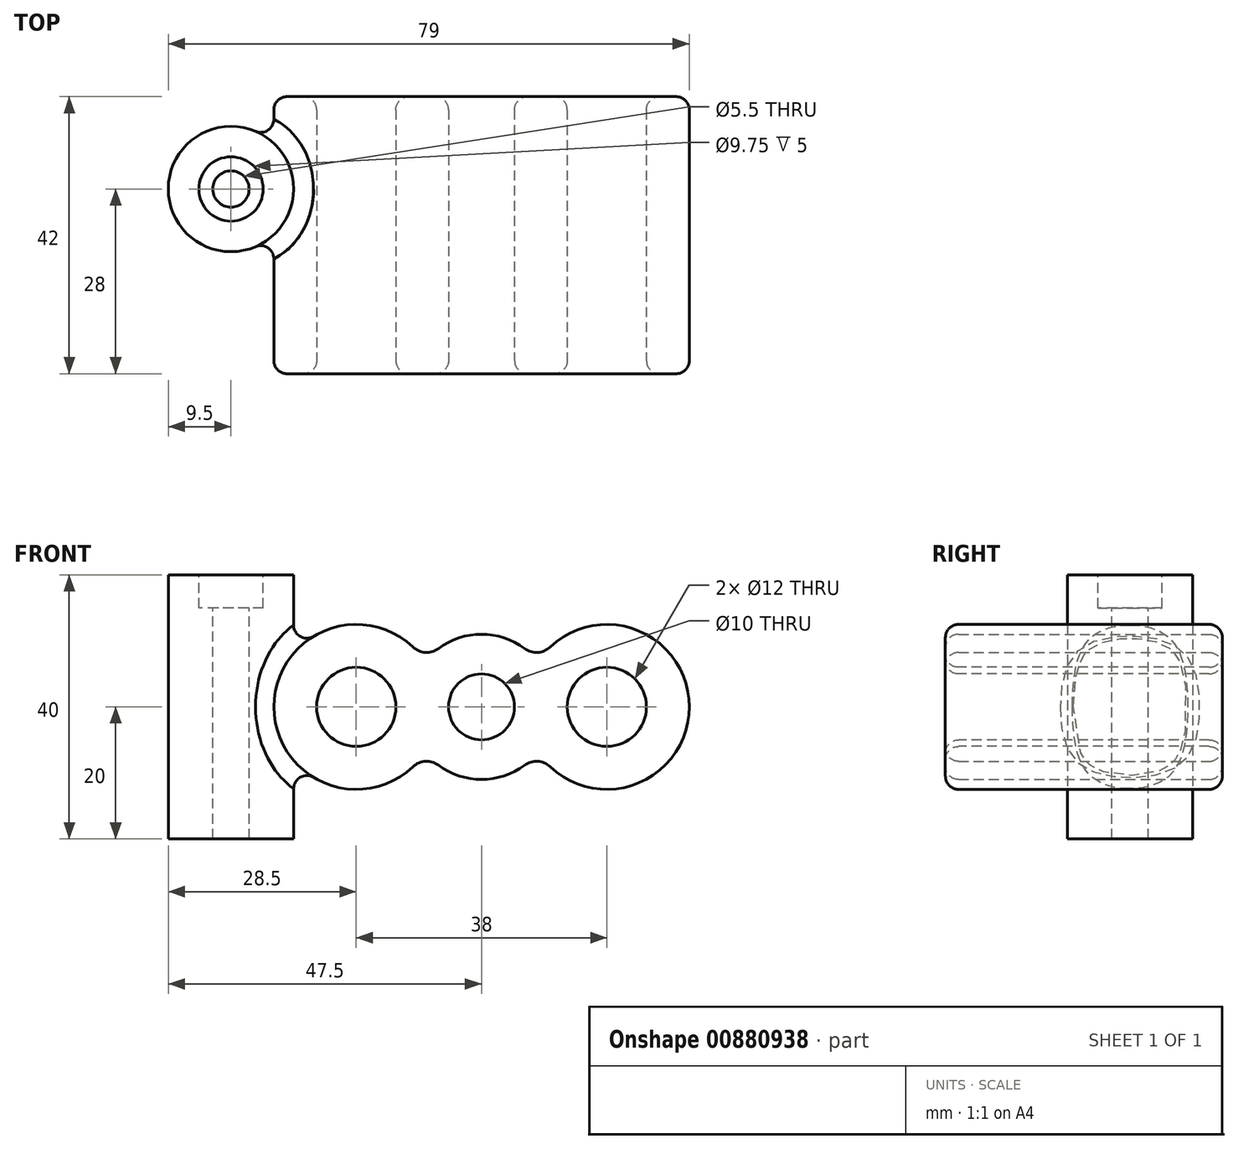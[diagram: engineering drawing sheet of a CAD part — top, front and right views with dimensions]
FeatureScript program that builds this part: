
annotation { "Feature Type Name" : "Feature", "Feature Type Description" : "" }
export const myFeature = defineFeature(function(context is Context, id is Id, definition is map)
    precondition{}
    {
        {
            var Q0;
            Q0=qCreatedBy(makeId("Front.planeOp"),FACE);
            var sketch = newSketch(context, id + "F0", { "sketchPlane" : qUnion([Q0])});
            skArc(sketch, "E0", {"start": v(-6.55, -8.84) * mm, "mid": v(0, -11) * mm, "end": v(6.55, -8.84) * mm});
            skArc(sketch, "E1", {"start": v(-10.4, 9.07) * mm, "mid": v(-31.5, 0) * mm, "end": v(-10.4, -9.07) * mm});
            skArc(sketch, "E2", {"start": v(10.4, -9.07) * mm, "mid": v(31.5, 0) * mm, "end": v(10.4, 9.07) * mm});
            skArc(sketch, "E3.trimOffspring", {"start": v(6.55, 8.84) * mm, "mid": v(0, 11) * mm, "end": v(-6.55, 8.84) * mm});
            skPoint(sketch, "E4.visualSharp", {"position": v(-8.57, -6.9) * mm});
            skArc(sketch, "E4.filletArc", {"start": v(-6.55, -8.84) * mm, "mid": v(-8.52, -8.25) * mm, "end": v(-10.4, -9.07) * mm});
            skPoint(sketch, "E5.visualSharp", {"position": v(8.57, -6.9) * mm});
            skArc(sketch, "E5.filletArc", {"start": v(10.4, -9.07) * mm, "mid": v(8.52, -8.25) * mm, "end": v(6.55, -8.84) * mm});
            skPoint(sketch, "E6.visualSharp", {"position": v(8.57, 6.9) * mm});
            skArc(sketch, "E6.filletArc", {"start": v(6.55, 8.84) * mm, "mid": v(8.52, 8.25) * mm, "end": v(10.4, 9.07) * mm});
            skPoint(sketch, "E7.visualSharp", {"position": v(-8.57, 6.9) * mm});
            skArc(sketch, "E7.filletArc", {"start": v(-10.4, 9.07) * mm, "mid": v(-8.52, 8.25) * mm, "end": v(-6.55, 8.84) * mm});
            skSolve(sketch);
        }
        {
            var Q0;
            Q0 = qSketchRegion(id + "F0", true);
            extrude(context, id + "F1", {"entities" : qUnion([Q0]), "depth" : 42 * mm, "offsetDistance" : 25 * mm});
        }
        {
            var Q0;
            Q0=makeQuery(id+"F1.opExtrude","CAP_FACE",FACE,{"disambiguationData":[OSD([sQuery(id+"F0.wireOp",EDGE,"E0"),sQuery(id+"F0.wireOp",EDGE,"E1"),sQuery(id+"F0.wireOp",EDGE,"E2"),sQuery(id+"F0.wireOp",EDGE,"E3.trimOffspring"),sQuery(id+"F0.wireOp",EDGE,"E4.filletArc"),sQuery(id+"F0.wireOp",EDGE,"E5.filletArc"),sQuery(id+"F0.wireOp",EDGE,"E6.filletArc"),sQuery(id+"F0.wireOp",EDGE,"E7.filletArc")])],"isStart":false});
            var sketch = newSketch(context, id + "F2", { "sketchPlane" : qUnion([Q0])});
            skCircle(sketch, "E8", {"center": v(0, 0) * mm, "radius": 5 * mm});
            skCircle(sketch, "E9", {"center": v(-19, 0) * mm, "radius": 6 * mm});
            skCircle(sketch, "E10", {"center": v(19, 0) * mm, "radius": 6 * mm});
            skSolve(sketch);
        }
        {
            var Q0;
            Q0 = qSketchRegion(id + "F2", true);
            extrude(context, id + "F3", {"entities" : qUnion([Q0]), "operationType" : NewBodyOperationType.REMOVE, "endBound" : BoundingType.THROUGH_ALL, "oppositeDirection" : true, "depth" : 25 * mm, "offsetDistance" : 25 * mm});
        }
        {
            var Q0;
            Q0=qCreatedBy(makeId("Top.planeOp"),FACE);
            var sketch = newSketch(context, id + "F4", { "sketchPlane" : qUnion([Q0])});
            skCircle(sketch, "E11", {"center": v(-38, -14) * mm, "radius": 9.5 * mm});
            skSolve(sketch);
        }
        {
            var Q0;
            Q0 = qSketchRegion(id + "F4", true);
            extrude(context, id + "F5", {"entities" : qUnion([Q0]), "operationType" : NewBodyOperationType.ADD, "endBound" : BoundingType.SYMMETRIC, "depth" : 40 * mm, "offsetDistance" : 25 * mm});
        }
        {
            var Q0;
            Q0=makeQuery(id+"F5.opExtrude","CAP_FACE",FACE,{"disambiguationData":[OSD([sQuery(id+"F4.wireOp",EDGE,"E11")])],"isStart":false});
            var sketch = newSketch(context, id + "F6", { "sketchPlane" : qUnion([Q0])});
            skPoint(sketch, "E12", {"position": v(-38, -14) * mm});
            skSolve(sketch);
        }
        {
            var Q0;
            Q0=sQuery(id+"F6.wireOp",VERTEX,"E12");
            var Q1;
            Q1=makeQuery(id+"F1.opExtrude","SWEPT_BODY",BODY,{"disambiguationData":[OSD([sQuery(id+"F0.wireOp",EDGE,"E0"),sQuery(id+"F0.wireOp",EDGE,"E1"),sQuery(id+"F0.wireOp",EDGE,"E2"),sQuery(id+"F0.wireOp",EDGE,"E3.trimOffspring"),sQuery(id+"F0.wireOp",EDGE,"E4.filletArc"),sQuery(id+"F0.wireOp",EDGE,"E5.filletArc"),sQuery(id+"F0.wireOp",EDGE,"E6.filletArc"),sQuery(id+"F0.wireOp",EDGE,"E7.filletArc")])]});
            hole(context, id + "F7", {"style" : HoleStyle.C_BORE, "endStyle" : HoleEndStyle.THROUGH, "standardTappedOrClearance" : lookupTablePath({ "fit" : "Normal", "standard" : "ISO", "size" : "M5", "type" : "Clearance" }), "standardBlindInLast" : lookupTablePath({ "fit" : "Normal", "standard" : "ISO", "engagement" : "75%", "pitch" : "0.8 mm", "size" : "M5", "type" : "Clearance & tapped" }), "holeDiameter" : 5.5 * mm, "cBoreDiameter" : 9.75 * mm, "cBoreDepth" : 5 * mm, "majorDiameter" : 5 * mm, "isTappedThrough" : true, "tappedDepth" : 12 * mm, "tapClearance" : 3, "locations" : qUnion([Q0]), "scope" : qUnion([Q1])});
        }
        {
            var Q0;
            Q0=makeQuery(id+"F5.boolean.opBoolean","INTERSECT",EDGE,{"derivedFrom":[makeQuery(id+"F1.opExtrude","SWEPT_FACE",FACE,{"disambiguationData":[OSD([sQuery(id+"F0.wireOp",EDGE,"E1")])]}),makeQuery(id+"F5.opExtrude","SWEPT_FACE",FACE,{"disambiguationData":[OSD([sQuery(id+"F4.wireOp",EDGE,"E11")])]})]});
            var Q1;
            Q1=makeQuery(id+"F1.opExtrude","CAP_FACE",FACE,{"disambiguationData":[OSD([sQuery(id+"F0.wireOp",EDGE,"E0"),sQuery(id+"F0.wireOp",EDGE,"E1"),sQuery(id+"F0.wireOp",EDGE,"E2"),sQuery(id+"F0.wireOp",EDGE,"E3.trimOffspring"),sQuery(id+"F0.wireOp",EDGE,"E4.filletArc"),sQuery(id+"F0.wireOp",EDGE,"E5.filletArc"),sQuery(id+"F0.wireOp",EDGE,"E6.filletArc"),sQuery(id+"F0.wireOp",EDGE,"E7.filletArc")])],"isStart":false});
            var Q2;
            Q2=makeQuery(id+"F1.opExtrude","CAP_FACE",FACE,{"disambiguationData":[OSD([sQuery(id+"F0.wireOp",EDGE,"E0"),sQuery(id+"F0.wireOp",EDGE,"E1"),sQuery(id+"F0.wireOp",EDGE,"E2"),sQuery(id+"F0.wireOp",EDGE,"E3.trimOffspring"),sQuery(id+"F0.wireOp",EDGE,"E4.filletArc"),sQuery(id+"F0.wireOp",EDGE,"E5.filletArc"),sQuery(id+"F0.wireOp",EDGE,"E6.filletArc"),sQuery(id+"F0.wireOp",EDGE,"E7.filletArc")])],"isStart":true});
            fillet(context, id + "F8", {"entities" : qUnion([Q0, Q1, Q2]), "radius" : 2 * mm, "tangentPropagation" : true, "allowEdgeOverflow" : false});
        }
    });
